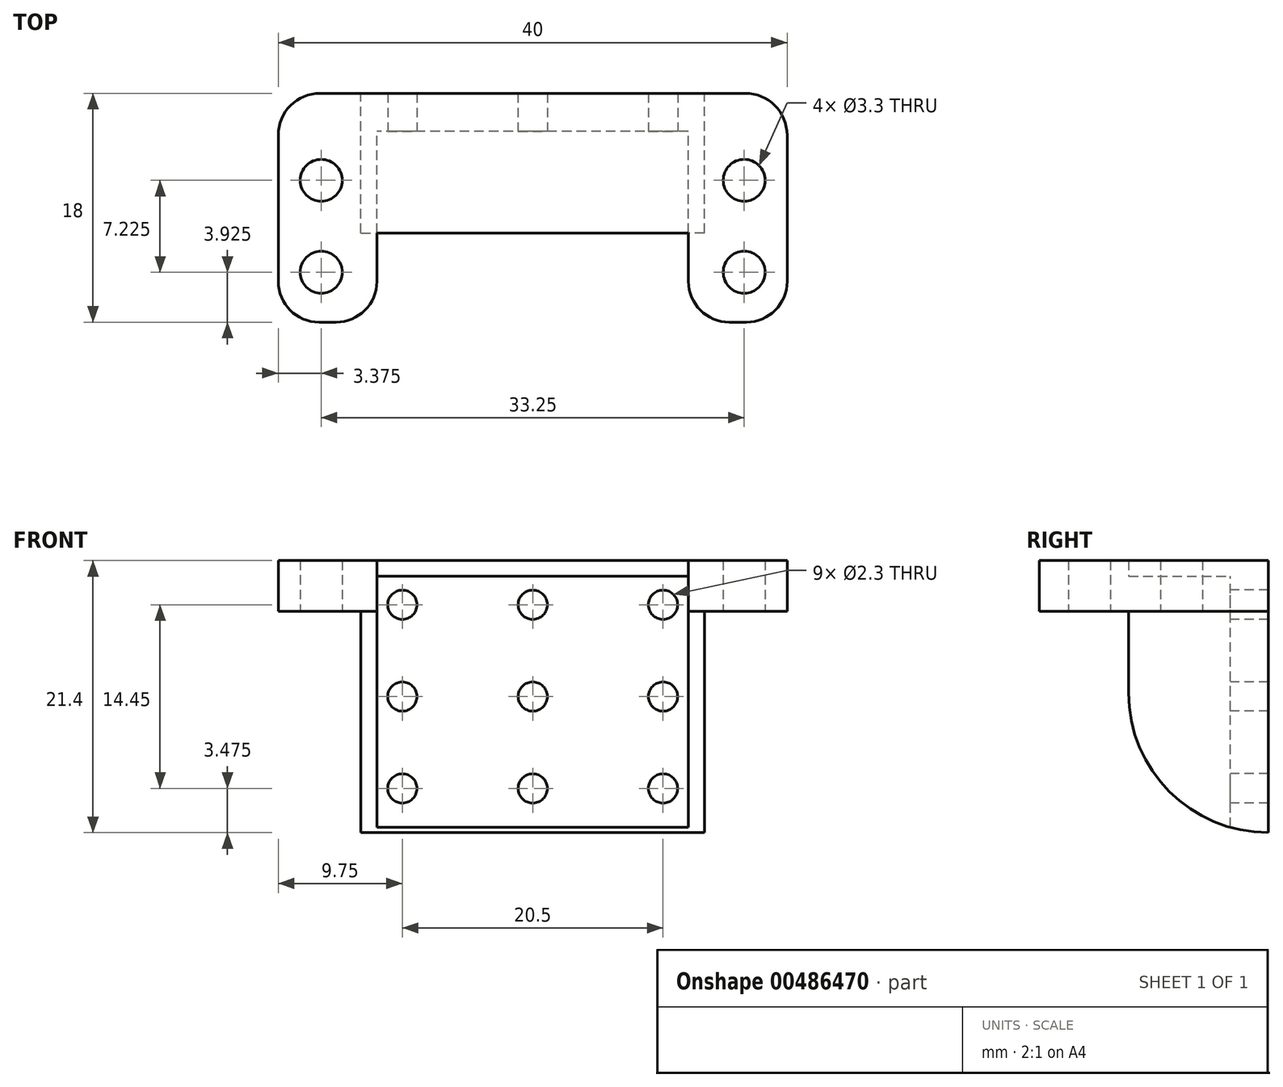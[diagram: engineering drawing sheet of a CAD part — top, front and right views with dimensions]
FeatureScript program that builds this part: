
annotation { "Feature Type Name" : "Feature", "Feature Type Description" : "" }
export const myFeature = defineFeature(function(context is Context, id is Id, definition is map)
    precondition{}
    {
        {
            var Q0;
            Q0=qCreatedBy(makeId("Front.planeOp"),FACE);
            var sketch = newSketch(context, id + "F0", { "sketchPlane" : qUnion([Q0])});
            skLineSegment(sketch, "E0.bottom", {"start": v(-13.5, -10.7) * mm, "end": v(13.5, -10.7) * mm});
            skLineSegment(sketch, "E0.top", {"start": v(-13.5, 10.7) * mm, "end": v(13.5, 10.7) * mm});
            skLineSegment(sketch, "E0.left", {"start": v(-13.5, -10.7) * mm, "end": v(-13.5, 10.7) * mm});
            skLineSegment(sketch, "E0.right", {"start": v(13.5, -10.7) * mm, "end": v(13.5, 10.7) * mm});
            skSolve(sketch);
        }
        {
            var Q0;
            Q0=makeQuery(id+"F0.imprint","IMPRINT",FACE,{"disambiguationData":[TD([[makeQuery(id+"F0.imprint","IMPRINT",EDGE,{"derivedFrom":sQuery(id+"F0.wireOp",EDGE,"E0.bottom")}),1.0]])]});
            extrude(context, id + "F1", {"entities" : qUnion([Q0]), "oppositeDirection" : true, "depth" : 3 * mm, "offsetDistance" : 25 * mm});
        }
        {
            var Q0;
            Q0=qCreatedBy(makeId("Front.planeOp"),FACE);
            var sketch = newSketch(context, id + "F2", { "sketchPlane" : qUnion([Q0])});
            skCircle(sketch, "E1", {"center": v(0, 7.22) * mm, "radius": 1.15 * mm});
            skCircle(sketch, "E2", {"center": v(0, 0) * mm, "radius": 1.15 * mm});
            skCircle(sketch, "E3.MirrorC", {"center": v(0, -7.22) * mm, "radius": 1.15 * mm});
            skCircle(sketch, "E4.1.0.0", {"center": v(10.25, 0) * mm, "radius": 1.15 * mm});
            skCircle(sketch, "E4.1.0.1", {"center": v(10.25, 7.22) * mm, "radius": 1.15 * mm});
            skCircle(sketch, "E4.1.0.2", {"center": v(10.25, -7.22) * mm, "radius": 1.15 * mm});
            skLineSegment(sketch, "E4.direction1", {"start": v(0, -7.22) * mm, "end": v(10.25, -7.22) * mm, "construction": true});
            skCircle(sketch, "E5.1.0.0", {"center": v(-10.25, -7.22) * mm, "radius": 1.15 * mm});
            skCircle(sketch, "E5.1.0.1", {"center": v(-10.25, 0) * mm, "radius": 1.15 * mm});
            skCircle(sketch, "E5.1.0.2", {"center": v(-10.25, 7.22) * mm, "radius": 1.15 * mm});
            skLineSegment(sketch, "E5.direction1", {"start": v(0, -7.22) * mm, "end": v(-10.25, -7.22) * mm, "construction": true});
            skSolve(sketch);
        }
        {
            var Q0;
            Q0 = qSketchRegion(id + "F2", true);
            extrude(context, id + "F3", {"entities" : qUnion([Q0]), "operationType" : NewBodyOperationType.REMOVE, "endBound" : BoundingType.THROUGH_ALL, "oppositeDirection" : true, "depth" : 25 * mm, "offsetDistance" : 25 * mm});
        }
        {
            var Q0;
            Q0=qCreatedBy(makeId("Front.planeOp"),FACE);
            var sketch = newSketch(context, id + "F4", { "sketchPlane" : qUnion([Q0])});
            skLineSegment(sketch, "E6", {"start": v(0, 10.7) * mm, "end": v(20, 10.7) * mm});
            skLineSegment(sketch, "E7", {"start": v(20, 6.7) * mm, "end": v(20, 10.7) * mm});
            skLineSegment(sketch, "E8", {"start": v(20, 6.7) * mm, "end": v(13.5, 6.7) * mm});
            skLineSegment(sketch, "E9", {"start": v(13.5, -10.7) * mm, "end": v(13.5, 6.7) * mm});
            skLineSegment(sketch, "E10", {"start": v(13.5, -10.7) * mm, "end": v(12.25, -10.7) * mm});
            skLineSegment(sketch, "E11", {"start": v(12.25, 9.47) * mm, "end": v(12.25, -10.7) * mm});
            skLineSegment(sketch, "E12", {"start": v(12.25, 9.47) * mm, "end": v(0, 9.47) * mm});
            skLineSegment(sketch, "E13.MirrorCS", {"start": v(-12.25, 9.47) * mm, "end": v(0, 9.47) * mm});
            skLineSegment(sketch, "E14.MirrorCS", {"start": v(0, 10.7) * mm, "end": v(-20, 10.7) * mm});
            skLineSegment(sketch, "E15.MirrorCS", {"start": v(-13.5, -10.7) * mm, "end": v(-13.5, 6.7) * mm});
            skLineSegment(sketch, "E16.MirrorCS", {"start": v(-12.25, 9.47) * mm, "end": v(-12.25, -10.7) * mm});
            skLineSegment(sketch, "E17.MirrorCS", {"start": v(-20, 6.7) * mm, "end": v(-13.5, 6.7) * mm});
            skLineSegment(sketch, "E18.MirrorCS", {"start": v(-20, 6.7) * mm, "end": v(-20, 10.7) * mm});
            skLineSegment(sketch, "E19.MirrorCS", {"start": v(-13.5, -10.7) * mm, "end": v(-12.25, -10.7) * mm});
            skSolve(sketch);
        }
        {
            var Q0;
            Q0 = qSketchRegion(id + "F4", true);
            extrude(context, id + "F5", {"entities" : qUnion([Q0]), "operationType" : NewBodyOperationType.ADD, "depth" : 8 * mm, "offsetDistance" : 25 * mm, "hasSecondDirection" : true, "secondDirectionOppositeDirection" : true, "secondDirectionDepth" : 3 * mm});
        }
        {
            var Q0;
            Q0=makeQuery(id+"F5.opExtrude","CAP_FACE",FACE,{"disambiguationData":[OSD([sQuery(id+"F4.wireOp",EDGE,"E6"),sQuery(id+"F4.wireOp",EDGE,"E7"),sQuery(id+"F4.wireOp",EDGE,"E8"),sQuery(id+"F4.wireOp",EDGE,"E9"),sQuery(id+"F4.wireOp",EDGE,"E10"),sQuery(id+"F4.wireOp",EDGE,"E11"),sQuery(id+"F4.wireOp",EDGE,"E12"),sQuery(id+"F4.wireOp",EDGE,"E13.MirrorCS"),sQuery(id+"F4.wireOp",EDGE,"E14.MirrorCS"),sQuery(id+"F4.wireOp",EDGE,"E15.MirrorCS"),sQuery(id+"F4.wireOp",EDGE,"E16.MirrorCS"),sQuery(id+"F4.wireOp",EDGE,"E17.MirrorCS"),sQuery(id+"F4.wireOp",EDGE,"E18.MirrorCS"),sQuery(id+"F4.wireOp",EDGE,"E19.MirrorCS")])],"isStart":false});
            var sketch = newSketch(context, id + "F6", { "sketchPlane" : qUnion([Q0])});
            skLineSegment(sketch, "E20.bottom", {"start": v(20, 6.7) * mm, "end": v(12.25, 6.7) * mm});
            skLineSegment(sketch, "E20.top", {"start": v(20, 10.7) * mm, "end": v(12.25, 10.7) * mm});
            skLineSegment(sketch, "E20.left", {"start": v(20, 6.7) * mm, "end": v(20, 10.7) * mm});
            skLineSegment(sketch, "E20.right", {"start": v(12.25, 6.7) * mm, "end": v(12.25, 10.7) * mm});
            skLineSegment(sketch, "E21.bottom", {"start": v(-20, 6.7) * mm, "end": v(-12.25, 6.7) * mm});
            skLineSegment(sketch, "E21.top", {"start": v(-20, 10.7) * mm, "end": v(-12.25, 10.7) * mm});
            skLineSegment(sketch, "E21.left", {"start": v(-20, 6.7) * mm, "end": v(-20, 10.7) * mm});
            skLineSegment(sketch, "E21.right", {"start": v(-12.25, 6.7) * mm, "end": v(-12.25, 10.7) * mm});
            skSolve(sketch);
        }
        {
            var Q0;
            Q0 = qSketchRegion(id + "F6", true);
            extrude(context, id + "F7", {"entities" : qUnion([Q0]), "operationType" : NewBodyOperationType.ADD, "depth" : 7 * mm, "offsetDistance" : 25 * mm});
        }
        {
            var Q0;
            Q0=makeQuery(id+"F5.opExtrude","SWEPT_FACE",FACE,{"disambiguationData":[OSD([sQuery(id+"F4.wireOp",EDGE,"E17.MirrorCS")])]});
            var sketch = newSketch(context, id + "F8", { "sketchPlane" : qUnion([Q0])});
            skCircle(sketch, "E22", {"center": v(-16.62, 3.85) * mm, "radius": 1.65 * mm});
            skCircle(sketch, "E23.MirrorC", {"center": v(16.62, 3.85) * mm, "radius": 1.65 * mm});
            skCircle(sketch, "E24.1.0.0", {"center": v(16.62, 11.08) * mm, "radius": 1.65 * mm});
            skCircle(sketch, "E24.1.0.1", {"center": v(-16.62, 11.07) * mm, "radius": 1.65 * mm});
            skLineSegment(sketch, "E24.direction1", {"start": v(16.62, 3.85) * mm, "end": v(16.62, 11.08) * mm, "construction": true});
            skSolve(sketch);
        }
        {
            var Q0;
            Q0 = qSketchRegion(id + "F8", true);
            extrude(context, id + "F9", {"entities" : qUnion([Q0]), "operationType" : NewBodyOperationType.REMOVE, "oppositeDirection" : true, "depth" : 25 * mm, "offsetDistance" : 25 * mm});
        }
        {
            var Q0;
            Q0=makeQuery(id+"F5.opExtrude","CAP_EDGE",EDGE,{"disambiguationData":[OSD([sQuery(id+"F4.wireOp",EDGE,"E10")])],"isStart":false});
            var Q1;
            Q1=makeQuery(id+"F5.opExtrude","CAP_EDGE",EDGE,{"disambiguationData":[OSD([sQuery(id+"F4.wireOp",EDGE,"E19.MirrorCS")])],"isStart":false});
            fillet(context, id + "F10", {"entities" : qUnion([Q0, Q1]), "radius" : 11 * mm, "tangentPropagation" : true, "allowEdgeOverflow" : false});
        }
        {
            var Q0;
            Q0=makeQuery(id+"F5.opExtrude","CAP_EDGE",EDGE,{"disambiguationData":[OSD([sQuery(id+"F4.wireOp",EDGE,"E7")])],"isStart":true});
            var Q1;
            Q1=makeQuery(id+"F5.opExtrude","CAP_EDGE",EDGE,{"disambiguationData":[OSD([sQuery(id+"F4.wireOp",EDGE,"E18.MirrorCS")])],"isStart":true});
            fillet(context, id + "F11", {"entities" : qUnion([Q0, Q1]), "radius" : 3.3 * mm, "tangentPropagation" : true, "allowEdgeOverflow" : false});
        }
        {
            var Q0;
            Q0=makeQuery(id+"F7.opExtrude","CAP_EDGE",EDGE,{"disambiguationData":[OSD([sQuery(id+"F6.wireOp",EDGE,"E20.left")])],"isStart":false});
            var Q1;
            Q1=makeQuery(id+"F7.opExtrude","CAP_EDGE",EDGE,{"disambiguationData":[OSD([sQuery(id+"F6.wireOp",EDGE,"E20.right")])],"isStart":false});
            var Q2;
            Q2=makeQuery(id+"F7.opExtrude","CAP_EDGE",EDGE,{"disambiguationData":[OSD([sQuery(id+"F6.wireOp",EDGE,"E21.right")])],"isStart":false});
            var Q3;
            Q3=makeQuery(id+"F7.opExtrude","CAP_EDGE",EDGE,{"disambiguationData":[OSD([sQuery(id+"F6.wireOp",EDGE,"E21.left")])],"isStart":false});
            fillet(context, id + "F12", {"entities" : qUnion([Q0, Q1, Q2, Q3]), "radius" : 3.2 * mm, "tangentPropagation" : true, "allowEdgeOverflow" : false});
        }
    });
